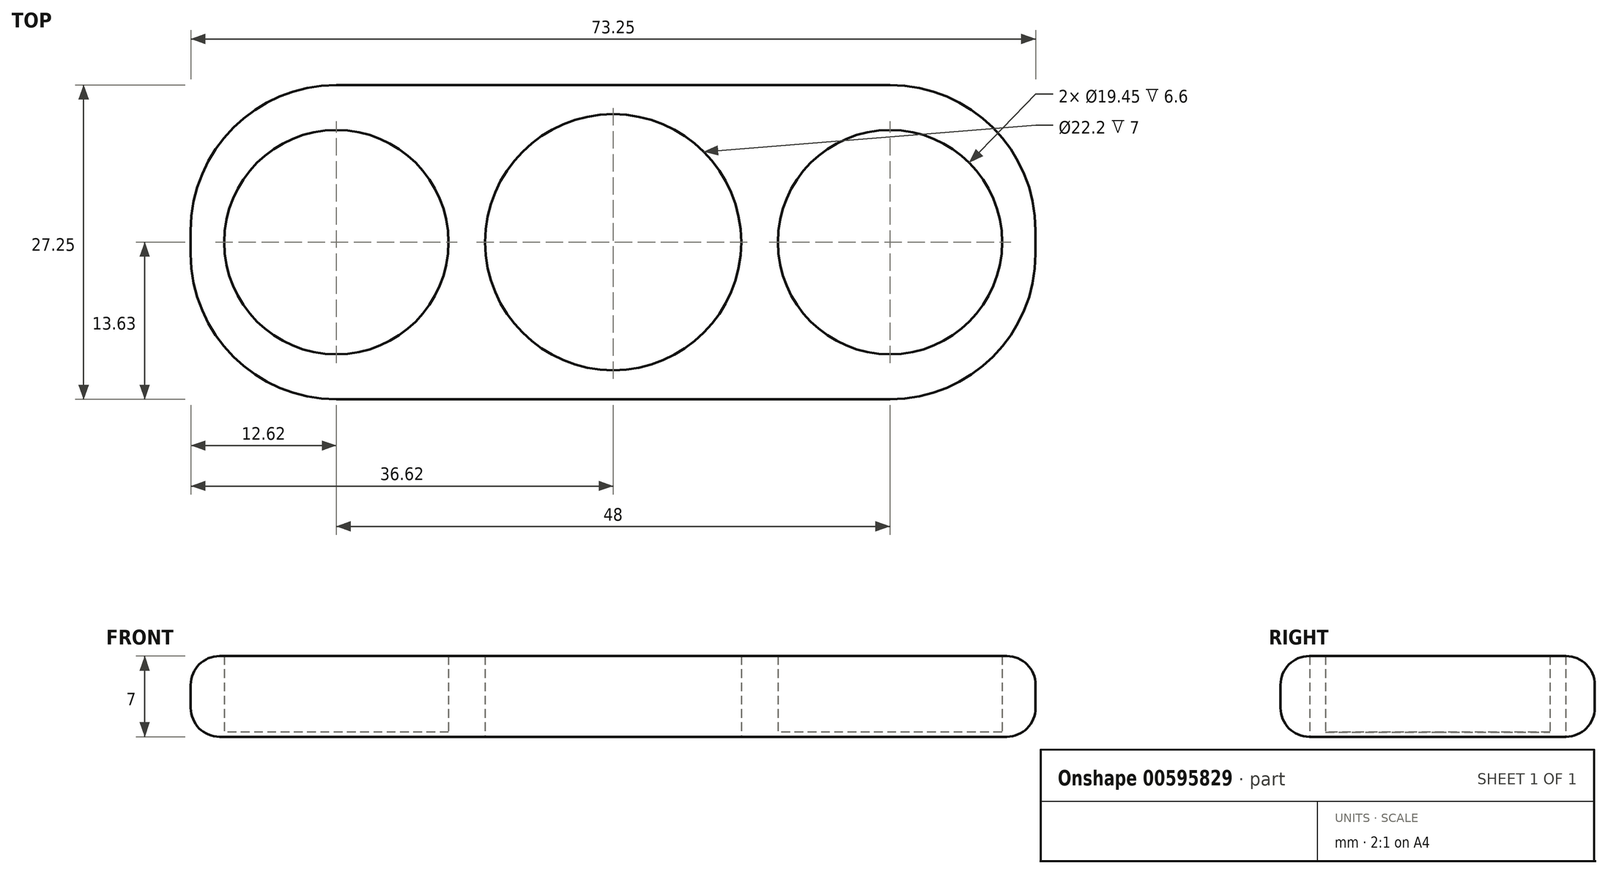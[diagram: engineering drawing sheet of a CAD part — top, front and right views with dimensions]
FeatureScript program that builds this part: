
annotation { "Feature Type Name" : "Feature", "Feature Type Description" : "" }
export const myFeature = defineFeature(function(context is Context, id is Id, definition is map)
    precondition{}
    {
        {
            var Q0;
            Q0=qCreatedBy(makeId("Top.planeOp"),FACE);
            var sketch = newSketch(context, id + "F0", { "sketchPlane" : qUnion([Q0])});
            skCircle(sketch, "E0", {"center": v(0, 0) * mm, "radius": 11.1 * mm});
            skCircle(sketch, "E1", {"center": v(-24, 0) * mm, "radius": 9.72 * mm});
            skCircle(sketch, "E2", {"center": v(24, 0) * mm, "radius": 9.72 * mm});
            skLineSegment(sketch, "E3.bottom", {"start": v(-24, 13.62) * mm, "end": v(24, 13.63) * mm});
            skLineSegment(sketch, "E3.top", {"start": v(-24, -13.63) * mm, "end": v(24, -13.62) * mm});
            skLineSegment(sketch, "E3.left", {"start": v(-36.62, 1) * mm, "end": v(-36.62, -1) * mm});
            skLineSegment(sketch, "E3.right", {"start": v(36.62, 1) * mm, "end": v(36.62, -1) * mm});
            skPoint(sketch, "E4.visualSharp", {"position": v(-36.62, 13.62) * mm});
            skArc(sketch, "E4.filletArc", {"start": v(-24, 13.62) * mm, "mid": v(-32.93, 9.93) * mm, "end": v(-36.62, 1) * mm});
            skPoint(sketch, "E5.visualSharp", {"position": v(-36.62, -13.63) * mm});
            skArc(sketch, "E5.filletArc", {"start": v(-36.62, -1) * mm, "mid": v(-32.93, -9.93) * mm, "end": v(-24, -13.63) * mm});
            skPoint(sketch, "E6.visualSharp", {"position": v(36.62, 13.63) * mm});
            skArc(sketch, "E6.filletArc", {"start": v(36.62, 1) * mm, "mid": v(32.93, 9.93) * mm, "end": v(24, 13.63) * mm});
            skPoint(sketch, "E7.visualSharp", {"position": v(36.62, -13.62) * mm});
            skArc(sketch, "E7.filletArc", {"start": v(24, -13.62) * mm, "mid": v(32.93, -9.93) * mm, "end": v(36.62, -1) * mm});
            skSolve(sketch);
        }
        {
            var Q0;
            Q0 = qSketchRegion(id + "F0", true);
            extrude(context, id + "F1", {"entities" : qUnion([Q0]), "depth" : 7 * mm, "offsetDistance" : 25 * mm});
        }
        {
            var Q0;
            Q0=makeQuery(id+"F1.opExtrude","CAP_EDGE",EDGE,{"disambiguationData":[OSD([sQuery(id+"F0.wireOp",EDGE,"E3.top")])],"isStart":false});
            var Q1;
            Q1=makeQuery(id+"F1.opExtrude","CAP_EDGE",EDGE,{"disambiguationData":[OSD([sQuery(id+"F0.wireOp",EDGE,"E3.top")])],"isStart":true});
            fillet(context, id + "F2", {"entities" : qUnion([Q0, Q1]), "radius" : 2.5 * mm, "tangentPropagation" : true, "allowEdgeOverflow" : false});
        }
        {
            var Q0;
            Q0=qCreatedBy(makeId("Top.planeOp"),FACE);
            var sketch = newSketch(context, id + "F3", { "sketchPlane" : qUnion([Q0])});
            skCircle(sketch, "E8", {"center": v(-24, 0) * mm, "radius": 9.75 * mm});
            skCircle(sketch, "E9", {"center": v(24, 0) * mm, "radius": 9.75 * mm});
            skSolve(sketch);
        }
        {
            var Q0;
            Q0 = qSketchRegion(id + "F3", true);
            extrude(context, id + "F4", {"entities" : qUnion([Q0]), "operationType" : NewBodyOperationType.ADD, "depth" : .4 * mm, "offsetDistance" : 25 * mm});
        }
    });
